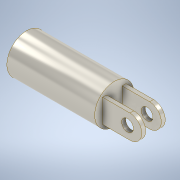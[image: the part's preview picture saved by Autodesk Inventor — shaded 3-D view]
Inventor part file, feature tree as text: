
AUTODESK INVENTOR PART (.ipt)
format: ipt  version: 2022 (Build 260153000, 153)  size: 150,528 bytes
history: native  units: in
note: dims shown in document units (in); Inventor stores cm internally (conversion verified against a paired STEP export)
features: extrude x4, sketch x4, fillet x1
ambient origin geometry x8: Origin, YZ Plane, XZ Plane, XY Plane, X Axis, Y Axis, Z Axis, Center Point
bodies: Solido1 (feature_tree)
feature tree (9):
  extrude  "Estrusione1"  Depth=0.3937in
  extrude  "Estrusione2"  Depth=0.8815in TaperAngle=0.0deg
  extrude  "Estrusione5"  Depth=0.2362in
  extrude  "Estrusione6"  Depth=0.2362in
  fillet  "Raccordo2"  Radius=0.3937in
  sketch  "Schizzo1"
  sketch  "Schizzo2"
  sketch  "Schizzo5"
  sketch  "Schizzo6"
